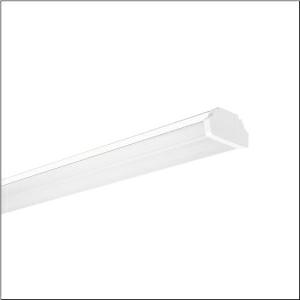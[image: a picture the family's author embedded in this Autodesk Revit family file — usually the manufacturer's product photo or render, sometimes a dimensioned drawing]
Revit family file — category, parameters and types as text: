
# Revit family: dus_r__31_gen_2_53bd812dv4a5c2_6be2
name_source: partatom
category: Lighting Fixtures
units: mm (PartAtom-declared; Revit-internal decimal feet)

## family parameters
Cut with Voids When Loaded = No
Host = Face
Light Source = No
Part Type = Normal
Room Calculation Point = No
Round Connector Dimension = Use Diameter
Shared = No

## types (1)
- --- (1 x LED, 10860 lm, 61.4 W, 4000K)
    Apparent Load = 61 VA
    CIE Flux Codes = 47 80 95 93 100
    Color Rendering = 80
    Color Temperature = 4000K
    Default Elevation = 1800 mm
    Description = DUS® 31 Gen.2, luminaire insert, of sheet steel, coil coated, white, length: 1.535mm, width: 81mm, height: 90mm, 5x system unit, system units: 307mm, LED rated luminous flux: 10.860lm, light colour: 840, control gear: DALI 2, control gear: ECG DALI, with plug, 5-pole, with phase selection, mains connection: 220..240V, AC, 50/60Hz, rated input power: 61W, through-wiring accessed according to module size, primary optical cover: cover, of PMMA, light emission: direct distribution, primary light characteristic: symmetric, protection rating (complete): IP20, protection rating (LED compartment): IP50, insulation class (complete): insulation class I (protective earthing), certification: CE, ENEC, VDE, UKCA, impact resistance: IK03, permissible ambient temperature for indoor applications: -25..+35°C, corresponds to IFS (International Featured Standards) requirements for safety and quality in the food industry, reducing of maximum allowable ambient temperature of 5°C with ceiling mounting, packaging unit: 1 piece
    Height = 95 mm
    Lamp = 1 x LED
    Lamp Light Flux = 10860 lm
    Lamp Power = 61.4 W
    Lamp count = 1
    Length = 1535 mm
    Luminous efficacy = 177 lm/W
    Manufacturer = Siteco
    ModVariant = No
    Model = 53BD812DV4A5C2
    Mounting Place = Ceiling
    Mounting Type = Pendant
    Number of Poles = 1
    OnlyDefault = Yes
    Power Factor = 1
    Product Name = DUS® 31 Gen.2
    Product group = luminaire insert
    ProductGroupID = 901
    Protection Class = Protection class I
    Protection Degree = IP 20
    RLX_Detail_Level = 1
    RLX_Emergency_Light_Flux = 0 lm
    RLX_Emergency_Type = 0
    RLX_Emergency_Type_DB = No
    RlxData = <blob elided: 32073 chars, md5=94daca81>
    Socket = socket
    Standby Power = 0 W
    System Light Flux = 10860 lm
    System Power = 61 W
    Type Comments = factory setting: luminous flux: 100 % | dim-lin: 254 | 418 mA
    Type Image = l_1319596.jpg
    URL = http://relux.com
    VarID = @adj_010213
    Voltage = 0 V
    Weight = 0.00 kg
    Width = 81 mm

## geometry (parser evidence)
native form markers: Blend x4, Sweep x12
no freeform markers — native parametric forms only
